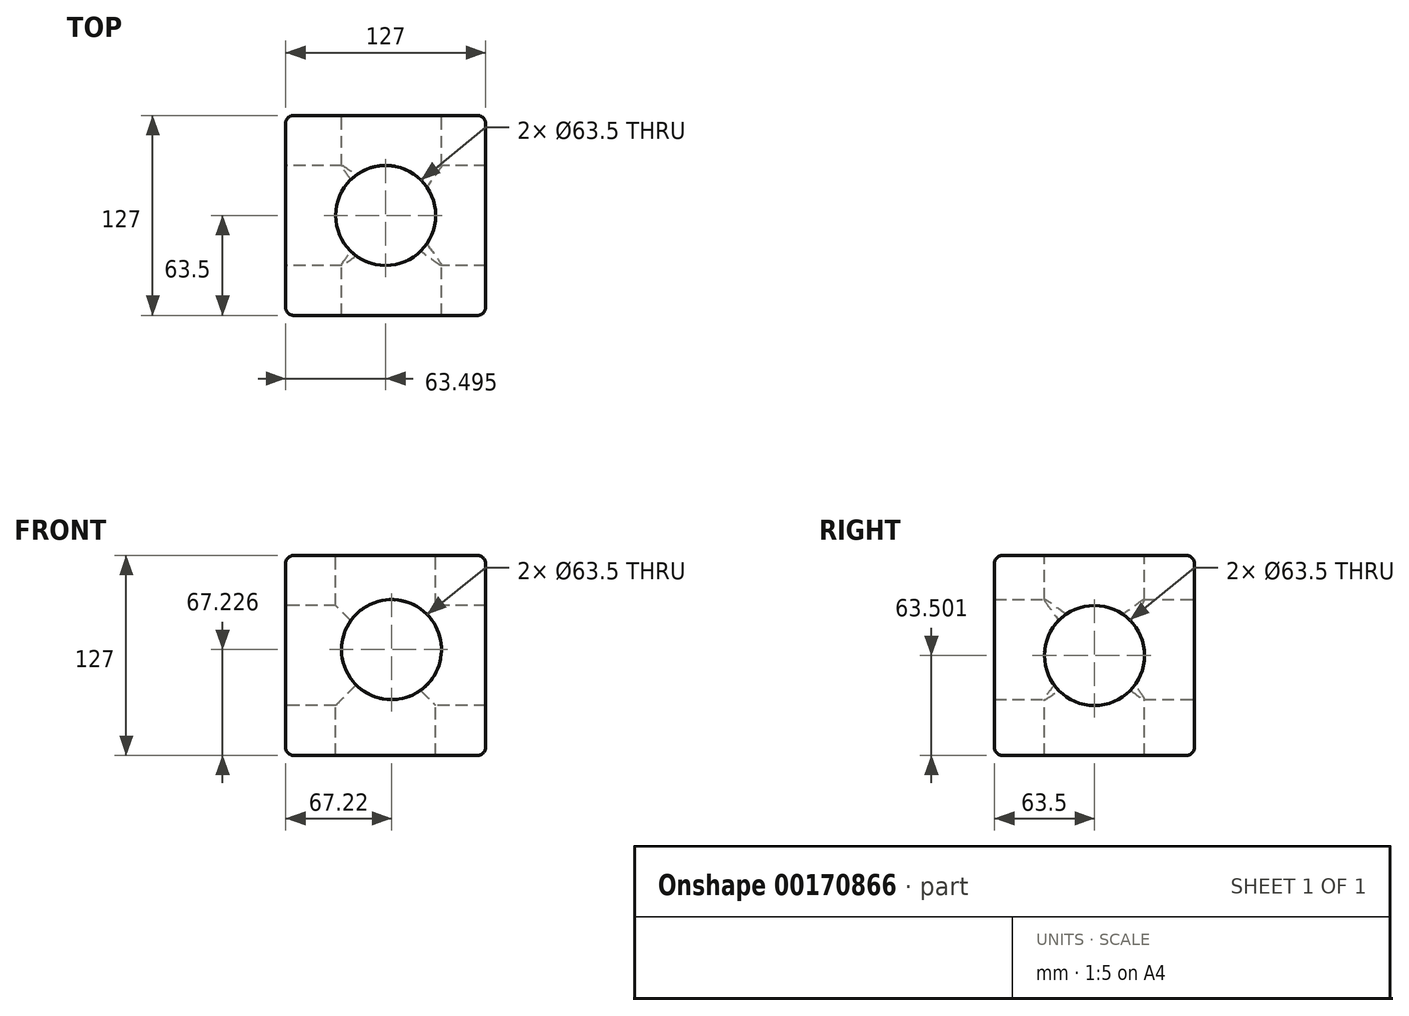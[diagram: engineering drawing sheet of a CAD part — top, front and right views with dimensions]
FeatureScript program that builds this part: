
annotation { "Feature Type Name" : "Feature", "Feature Type Description" : "" }
export const myFeature = defineFeature(function(context is Context, id is Id, definition is map)
    precondition{}
    {
        {
            var Q0;
            Q0=qCreatedBy(makeId("Front.planeOp"),FACE);
            var sketch = newSketch(context, id + "F0", { "sketchPlane" : qUnion([Q0])});
            skLineSegment(sketch, "E0.bottom", {"start": v(-67.22, 46.06) * mm, "end": v(59.78, 46.06) * mm});
            skLineSegment(sketch, "E0.top", {"start": v(-67.22, -80.94) * mm, "end": v(59.78, -80.94) * mm});
            skLineSegment(sketch, "E0.left", {"start": v(-67.22, 46.06) * mm, "end": v(-67.22, -80.94) * mm});
            skLineSegment(sketch, "E0.right", {"start": v(59.78, 46.06) * mm, "end": v(59.78, -80.94) * mm});
            skSolve(sketch);
        }
        {
            var Q0;
            Q0 = qSketchRegion(id + "F0", true);
            extrude(context, id + "F1", {"entities" : qUnion([Q0]), "depth" : 127 * mm});
        }
        {
            var Q0;
            Q0=makeQuery(id+"F1.opExtrude","SWEPT_FACE",FACE,{"disambiguationData":[OSD([sQuery(id+"F0.wireOp",EDGE,"E0.bottom")])]});
            var sketch = newSketch(context, id + "F2", { "sketchPlane" : qUnion([Q0])});
            skLineSegment(sketch, "E1", {"start": v(-67.22, 0) * mm, "end": v(59.78, -127) * mm, "construction": true});
            skCircle(sketch, "E2", {"center": v(-3.72, -63.5) * mm, "radius": 31.75 * mm});
            skSolve(sketch);
        }
        {
            var Q0;
            Q0 = qSketchRegion(id + "F2", true);
            extrude(context, id + "F3", {"entities" : qUnion([Q0]), "operationType" : NewBodyOperationType.REMOVE, "endBound" : BoundingType.THROUGH_ALL, "oppositeDirection" : true, "depth" : 25.4 * mm});
        }
        {
            var Q0;
            Q0=makeQuery(id+"F1.opExtrude","CAP_FACE",FACE,{"disambiguationData":[OSD([sQuery(id+"F0.wireOp",EDGE,"E0.bottom"),sQuery(id+"F0.wireOp",EDGE,"E0.top"),sQuery(id+"F0.wireOp",EDGE,"E0.left"),sQuery(id+"F0.wireOp",EDGE,"E0.right")])],"isStart":true});
            var sketch = newSketch(context, id + "F4", { "sketchPlane" : qUnion([Q0])});
            skLineSegment(sketch, "E3", {"start": v(-59.78, 46.06) * mm, "end": v(67.22, -80.94) * mm, "construction": true});
            skCircle(sketch, "E4", {"center": v(0, -13.71) * mm, "radius": 31.75 * mm});
            skSolve(sketch);
        }
        {
            var Q0;
            Q0 = qSketchRegion(id + "F4", true);
            extrude(context, id + "F5", {"entities" : qUnion([Q0]), "operationType" : NewBodyOperationType.REMOVE, "endBound" : BoundingType.THROUGH_ALL, "oppositeDirection" : true, "depth" : 25.4 * mm});
        }
        {
            var Q0;
            Q0=makeQuery(id+"F1.opExtrude","SWEPT_FACE",FACE,{"disambiguationData":[OSD([sQuery(id+"F0.wireOp",EDGE,"E0.left")])]});
            var sketch = newSketch(context, id + "F6", { "sketchPlane" : qUnion([Q0])});
            skLineSegment(sketch, "E5", {"start": v(0, 46.06) * mm, "end": v(127, -80.94) * mm, "construction": true});
            skCircle(sketch, "E6", {"center": v(63.5, -17.44) * mm, "radius": 31.75 * mm});
            skSolve(sketch);
        }
        {
            var Q0;
            Q0 = qSketchRegion(id + "F6", true);
            extrude(context, id + "F7", {"entities" : qUnion([Q0]), "operationType" : NewBodyOperationType.REMOVE, "endBound" : BoundingType.THROUGH_ALL, "oppositeDirection" : true, "depth" : 25.4 * mm});
        }
        {
            var Q0;
            Q0=makeQuery(id+"F1.opExtrude","CAP_EDGE",EDGE,{"disambiguationData":[OSD([sQuery(id+"F0.wireOp",EDGE,"E0.top")])],"isStart":false});
            var Q1;
            Q1=makeQuery(id+"F1.opExtrude","CAP_EDGE",EDGE,{"disambiguationData":[OSD([sQuery(id+"F0.wireOp",EDGE,"E0.right")])],"isStart":false});
            var Q2;
            Q2=makeQuery(id+"F1.opExtrude","CAP_EDGE",EDGE,{"disambiguationData":[OSD([sQuery(id+"F0.wireOp",EDGE,"E0.left")])],"isStart":false});
            var Q3;
            Q3=makeQuery(id+"F1.opExtrude","CAP_EDGE",EDGE,{"disambiguationData":[OSD([sQuery(id+"F0.wireOp",EDGE,"E0.bottom")])],"isStart":false});
            var Q4;
            Q4=makeQuery(id+"F1.opExtrude","SWEPT_EDGE",EDGE,{"disambiguationData":[OSD([sQuery(id+"F0.wireOp",EDGE,"E0.bottom"),sQuery(id+"F0.wireOp",EDGE,"E0.left")])]});
            var Q5;
            Q5=makeQuery(id+"F1.opExtrude","CAP_EDGE",EDGE,{"disambiguationData":[OSD([sQuery(id+"F0.wireOp",EDGE,"E0.left")])],"isStart":true});
            var Q6;
            Q6=makeQuery(id+"F1.opExtrude","CAP_EDGE",EDGE,{"disambiguationData":[OSD([sQuery(id+"F0.wireOp",EDGE,"E0.bottom")])],"isStart":true});
            var Q7;
            Q7=makeQuery(id+"F1.opExtrude","SWEPT_EDGE",EDGE,{"disambiguationData":[OSD([sQuery(id+"F0.wireOp",EDGE,"E0.top"),sQuery(id+"F0.wireOp",EDGE,"E0.left")])]});
            var Q8;
            Q8=makeQuery(id+"F1.opExtrude","SWEPT_EDGE",EDGE,{"disambiguationData":[OSD([sQuery(id+"F0.wireOp",EDGE,"E0.top"),sQuery(id+"F0.wireOp",EDGE,"E0.right")])]});
            var Q9;
            Q9=makeQuery(id+"F1.opExtrude","CAP_EDGE",EDGE,{"disambiguationData":[OSD([sQuery(id+"F0.wireOp",EDGE,"E0.right")])],"isStart":true});
            var Q10;
            Q10=makeQuery(id+"F1.opExtrude","CAP_EDGE",EDGE,{"disambiguationData":[OSD([sQuery(id+"F0.wireOp",EDGE,"E0.top")])],"isStart":true});
            var Q11;
            Q11=makeQuery(id+"F1.opExtrude","SWEPT_EDGE",EDGE,{"disambiguationData":[OSD([sQuery(id+"F0.wireOp",EDGE,"E0.bottom"),sQuery(id+"F0.wireOp",EDGE,"E0.right")])]});
            fillet(context, id + "F8", {"entities" : qUnion([Q0, Q1, Q2, Q3, Q4, Q5, Q6, Q7, Q8, Q9, Q10, Q11]), "radius" : 5.08 * mm, "tangentPropagation" : true, "allowEdgeOverflow" : false});
        }
    });
